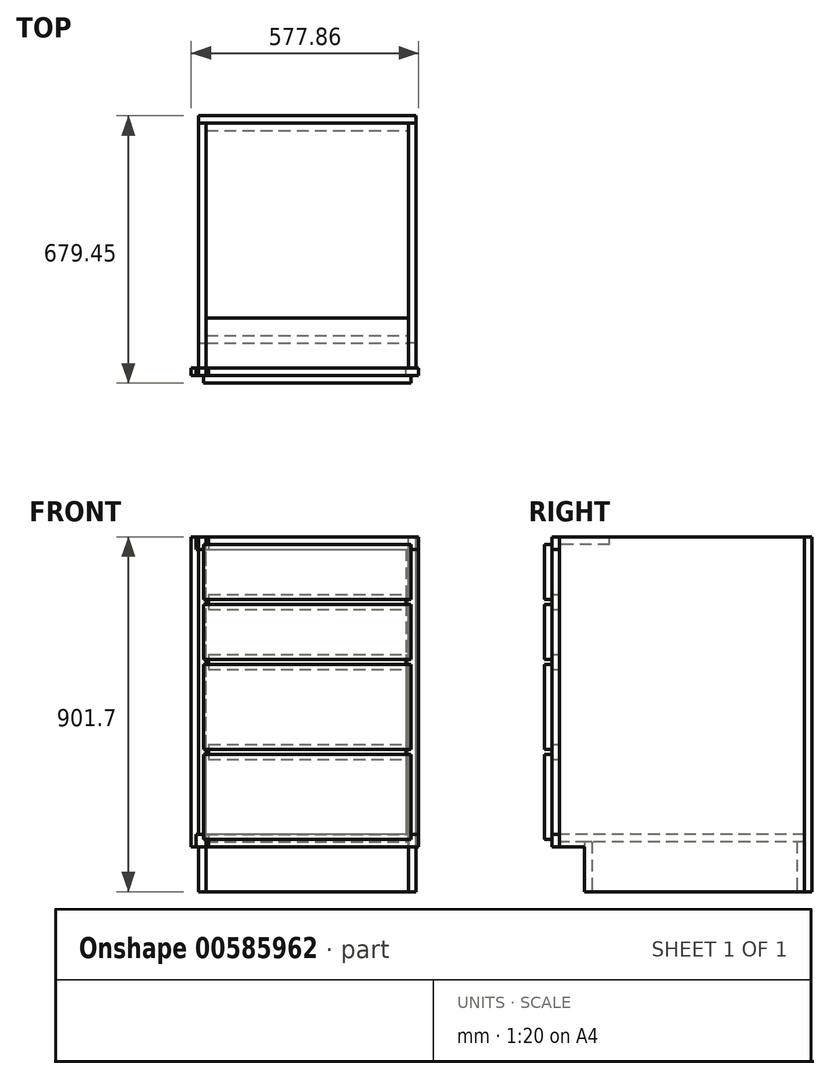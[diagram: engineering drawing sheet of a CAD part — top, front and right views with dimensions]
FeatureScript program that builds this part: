
annotation { "Feature Type Name" : "Feature", "Feature Type Description" : "" }
export const myFeature = defineFeature(function(context is Context, id is Id, definition is map)
    precondition{}
    {
        {
            var Q0;
            Q0=qCreatedBy(makeId("Top.planeOp"),FACE);
            var sketch = newSketch(context, id + "F0", { "sketchPlane" : qUnion([Q0])});
            skLineSegment(sketch, "E0.bottom", {"start": v(-257.18, 279.4) * mm, "end": v(257.18, 279.4) * mm});
            skLineSegment(sketch, "E0.top", {"start": v(-257.18, 260.35) * mm, "end": v(257.18, 260.35) * mm});
            skLineSegment(sketch, "E0.left", {"start": v(-257.18, 279.4) * mm, "end": v(-257.18, 260.35) * mm});
            skLineSegment(sketch, "E0.right", {"start": v(257.18, 279.4) * mm, "end": v(257.18, 260.35) * mm});
            skLineSegment(sketch, "E1.bottom", {"start": v(-257.18, -260.35) * mm, "end": v(257.18, -260.35) * mm});
            skLineSegment(sketch, "E1.top", {"start": v(-257.18, -279.4) * mm, "end": v(257.18, -279.4) * mm});
            skLineSegment(sketch, "E1.left", {"start": v(-257.18, -260.35) * mm, "end": v(-257.18, -279.4) * mm});
            skLineSegment(sketch, "E1.right", {"start": v(257.18, -260.35) * mm, "end": v(257.18, -279.4) * mm});
            skPoint(sketch, "E2", {"position": v(0, -260.35) * mm});
            skPoint(sketch, "E3", {"position": v(0, 260.35) * mm});
            skLineSegment(sketch, "E4", {"start": v(6.15, 279.4) * mm, "end": v(6.15, -279.4) * mm, "construction": true});
            skPoint(sketch, "E5", {"position": v(6.15, 0) * mm});
            skSolve(sketch);
        }
        {
            var Q0;
            Q0=makeQuery(id+"F0.imprint","IMPRINT",FACE,{"disambiguationData":[TD([[makeQuery(id+"F0.imprint","IMPRINT",EDGE,{"derivedFrom":sQuery(id+"F0.wireOp",EDGE,"E0.bottom")}),-1.0]])]});
            var Q1;
            Q1=makeQuery(id+"F0.imprint","IMPRINT",FACE,{"disambiguationData":[TD([[makeQuery(id+"F0.imprint","IMPRINT",EDGE,{"derivedFrom":sQuery(id+"F0.wireOp",EDGE,"E1.bottom")}),-1.0]])]});
            extrude(context, id + "F1", {"entities" : qUnion([Q0, Q1]), "depth" : 127 * mm, "offsetDistance" : 25.4 * mm});
        }
        {
            var Q0;
            Q0=makeQuery(id+"F1.opExtrude","SWEPT_FACE",FACE,{"disambiguationData":[OSD([sQuery(id+"F0.wireOp",EDGE,"E0.left")])]});
            var sketch = newSketch(context, id + "F2", { "sketchPlane" : qUnion([Q0])});
            skLineSegment(sketch, "E6.bottom", {"start": v(-279.4, 0) * mm, "end": v(342.9, 0) * mm});
            skLineSegment(sketch, "E6.top", {"start": v(-279.4, 901.7) * mm, "end": v(342.9, 901.7) * mm});
            skLineSegment(sketch, "E6.left", {"start": v(-279.4, 0) * mm, "end": v(-279.4, 901.7) * mm});
            skLineSegment(sketch, "E6.right", {"start": v(342.9, 0) * mm, "end": v(342.9, 901.7) * mm});
            skLineSegment(sketch, "E7.bottom", {"start": v(342.9, 0) * mm, "end": v(279.4, 0) * mm});
            skLineSegment(sketch, "E7.top", {"start": v(342.9, 114.3) * mm, "end": v(279.4, 114.3) * mm});
            skLineSegment(sketch, "E7.left", {"start": v(342.9, 0) * mm, "end": v(342.9, 114.3) * mm});
            skLineSegment(sketch, "E7.right", {"start": v(279.4, 0) * mm, "end": v(279.4, 114.3) * mm});
            skSolve(sketch);
        }
        {
            var Q0;
            {var subQ3=sQuery(id+"F2.wireOp",EDGE,"E6.top");Q0=makeQuery(id+"F2.imprint","IMPRINT",FACE,{"disambiguationData":[TD([[makeQuery(id+"F2.imprint","IMPRINT",EDGE,{"derivedFrom":subQ3}),-1.0]])]});}
            var Q1;
            {var subQ3=sQuery(id+"F0.wireOp",EDGE,"E0.left");var subQ5=makeQuery(id+"F1.opExtrude","CAP_EDGE",EDGE,{"disambiguationData":[OSD([subQ3])],"isStart":false});Q1=makeQuery(id+"F2.imprint","IMPRINT",FACE,{"disambiguationData":[TD([[makeQuery(id+"F2.imprint","IMPRINT",EDGE,{"derivedFrom":subQ5}),-1.0]])]});}
            extrude(context, id + "F3", {"entities" : qUnion([Q0, Q1]), "depth" : 19.05 * mm, "offsetDistance" : 25.4 * mm});
        }
        {
            var Q0;
            Q0=makeQuery(id+"F3.opExtrude","SWEPT_BODY",BODY,{"disambiguationData":[OSD([sQuery(id+"F2.wireOp",EDGE,"E6.bottom"),sQuery(id+"F2.wireOp",EDGE,"E6.top"),sQuery(id+"F2.wireOp",EDGE,"E6.left"),sQuery(id+"F2.wireOp",EDGE,"E6.right"),sQuery(id+"F2.wireOp",EDGE,"E7.top"),sQuery(id+"F2.wireOp",EDGE,"E7.right")])]});
            var Q1;
            Q1=qCreatedBy(makeId("Right.planeOp"),FACE);
            mirror(context, id + "F4", {"entities" : qUnion([Q0]), "mirrorPlane" : qUnion([Q1])});
        }
        {
            var Q0;
            Q0=makeQuery(id+"F1.opExtrude","CAP_FACE",FACE,{"disambiguationData":[OSD([sQuery(id+"F0.wireOp",EDGE,"E0.bottom"),sQuery(id+"F0.wireOp",EDGE,"E0.top"),sQuery(id+"F0.wireOp",EDGE,"E0.left"),sQuery(id+"F0.wireOp",EDGE,"E0.right")])],"isStart":false});
            var sketch = newSketch(context, id + "F5", { "sketchPlane" : qUnion([Q0])});
            skLineSegment(sketch, "E8.bottom", {"start": v(-257.18, 279.4) * mm, "end": v(257.18, 279.4) * mm});
            skLineSegment(sketch, "E8.top", {"start": v(-257.18, -342.9) * mm, "end": v(257.18, -342.9) * mm});
            skLineSegment(sketch, "E8.left", {"start": v(-257.18, 279.4) * mm, "end": v(-257.18, -342.9) * mm});
            skLineSegment(sketch, "E8.right", {"start": v(257.18, 279.4) * mm, "end": v(257.18, -342.9) * mm});
            skSolve(sketch);
        }
        {
            var Q0;
            {var subQ0=sQuery(id+"F5.wireOp",EDGE,"E8.top");Q0=makeQuery(id+"F5.imprint","IMPRINT",FACE,{"disambiguationData":[TD([[makeQuery(id+"F5.imprint","IMPRINT",EDGE,{"derivedFrom":subQ0}),1.0]])]});}
            var Q1;
            {var subQ0=sQuery(id+"F5.wireOp",EDGE,"E8.bottom");Q1=makeQuery(id+"F5.imprint","IMPRINT",FACE,{"disambiguationData":[TD([[makeQuery(id+"F5.imprint","IMPRINT",EDGE,{"derivedFrom":subQ0}),-1.0]])]});}
            extrude(context, id + "F6", {"entities" : qUnion([Q0, Q1]), "depth" : 19.05 * mm, "offsetDistance" : 25.4 * mm});
        }
        {
            var Q0;
            Q0=makeQuery(id+"F3.opExtrude","SWEPT_FACE",FACE,{"disambiguationData":[OSD([sQuery(id+"F2.wireOp",EDGE,"E6.top")])]});
            var sketch = newSketch(context, id + "F7", { "sketchPlane" : qUnion([Q0])});
            skLineSegment(sketch, "E9.bottom", {"start": v(-257.18, -342.9) * mm, "end": v(257.18, -342.9) * mm});
            skLineSegment(sketch, "E9.top", {"start": v(-257.18, -215.9) * mm, "end": v(257.18, -215.9) * mm});
            skLineSegment(sketch, "E9.left", {"start": v(-257.18, -342.9) * mm, "end": v(-257.18, -215.9) * mm});
            skLineSegment(sketch, "E9.right", {"start": v(257.18, -342.9) * mm, "end": v(257.18, -215.9) * mm});
            skLineSegment(sketch, "E10.bottom", {"start": v(-257.18, 279.4) * mm, "end": v(257.18, 279.4) * mm});
            skLineSegment(sketch, "E10.top", {"start": v(-257.18, 260.35) * mm, "end": v(257.18, 260.35) * mm});
            skLineSegment(sketch, "E10.left", {"start": v(-257.18, 279.4) * mm, "end": v(-257.18, 260.35) * mm});
            skLineSegment(sketch, "E10.right", {"start": v(257.18, 279.4) * mm, "end": v(257.18, 260.35) * mm});
            skSolve(sketch);
        }
        {
            var Q0;
            Q0=makeQuery(id+"F7.imprint","IMPRINT",FACE,{"disambiguationData":[TD([[makeQuery(id+"F7.imprint","IMPRINT",EDGE,{"derivedFrom":sQuery(id+"F7.wireOp",EDGE,"E9.bottom")}),1.0]])]});
            extrude(context, id + "F8", {"entities" : qUnion([Q0]), "oppositeDirection" : true, "depth" : 19.05 * mm, "offsetDistance" : 25.4 * mm});
        }
        {
            var Q0;
            Q0=makeQuery(id+"F3.opExtrude","SWEPT_FACE",FACE,{"disambiguationData":[OSD([sQuery(id+"F2.wireOp",EDGE,"E6.right")])]});
            var sketch = newSketch(context, id + "F9", { "sketchPlane" : qUnion([Q0])});
            skLineSegment(sketch, "E11.bottom", {"start": v(-282.58, 901.7) * mm, "end": v(282.58, 901.7) * mm});
            skLineSegment(sketch, "E11.top", {"start": v(-282.58, 869.95) * mm, "end": v(282.58, 869.95) * mm});
            skLineSegment(sketch, "E11.left", {"start": v(-282.58, 901.7) * mm, "end": v(-282.58, 869.95) * mm});
            skLineSegment(sketch, "E11.right", {"start": v(282.58, 901.7) * mm, "end": v(282.58, 869.95) * mm});
            skLineSegment(sketch, "E12.bottom", {"start": v(282.58, 114.3) * mm, "end": v(-282.58, 114.3) * mm});
            skLineSegment(sketch, "E12.top", {"start": v(282.58, 146.05) * mm, "end": v(-282.58, 146.05) * mm});
            skLineSegment(sketch, "E12.left", {"start": v(282.58, 114.3) * mm, "end": v(282.58, 146.05) * mm});
            skLineSegment(sketch, "E12.right", {"start": v(-282.58, 114.3) * mm, "end": v(-282.58, 146.05) * mm});
            skLineSegment(sketch, "E13.bottom", {"start": v(-282.58, 869.95) * mm, "end": v(-250.82, 869.95) * mm});
            skLineSegment(sketch, "E13.top", {"start": v(-282.58, 146.05) * mm, "end": v(-250.82, 146.05) * mm});
            skLineSegment(sketch, "E13.left", {"start": v(-282.58, 869.95) * mm, "end": v(-282.58, 146.05) * mm});
            skLineSegment(sketch, "E13.right", {"start": v(-250.82, 869.95) * mm, "end": v(-250.82, 146.05) * mm});
            skLineSegment(sketch, "E14.bottom", {"start": v(282.58, 869.95) * mm, "end": v(250.83, 869.95) * mm});
            skLineSegment(sketch, "E14.top", {"start": v(282.58, 146.05) * mm, "end": v(250.83, 146.05) * mm});
            skLineSegment(sketch, "E14.left", {"start": v(282.58, 869.95) * mm, "end": v(282.58, 146.05) * mm});
            skLineSegment(sketch, "E14.right", {"start": v(250.83, 869.95) * mm, "end": v(250.83, 146.05) * mm});
            skLineSegment(sketch, "E15.bottom", {"start": v(-250.82, 755.65) * mm, "end": v(250.83, 755.65) * mm});
            skLineSegment(sketch, "E15.top", {"start": v(-250.82, 717.55) * mm, "end": v(250.83, 717.55) * mm});
            skLineSegment(sketch, "E15.left", {"start": v(-250.82, 755.65) * mm, "end": v(-250.82, 717.55) * mm});
            skLineSegment(sketch, "E15.right", {"start": v(250.83, 755.65) * mm, "end": v(250.83, 717.55) * mm});
            skLineSegment(sketch, "E16.bottom", {"start": v(-250.83, 374.65) * mm, "end": v(250.83, 374.65) * mm});
            skLineSegment(sketch, "E16.top", {"start": v(-250.83, 336.55) * mm, "end": v(250.83, 336.55) * mm});
            skLineSegment(sketch, "E16.left", {"start": v(-250.82, 374.65) * mm, "end": v(-250.82, 336.55) * mm});
            skLineSegment(sketch, "E16.right", {"start": v(250.83, 374.65) * mm, "end": v(250.83, 336.55) * mm});
            skPoint(sketch, "E17", {"position": v(-250.83, 355.6) * mm});
            skLineSegment(sketch, "E18.bottom", {"start": v(-282.58, 901.7) * mm, "end": v(-250.82, 901.7) * mm});
            skLineSegment(sketch, "E18.right", {"start": v(-250.82, 901.7) * mm, "end": v(-250.82, 869.95) * mm});
            skLineSegment(sketch, "E19.top", {"start": v(282.58, 901.7) * mm, "end": v(250.83, 901.7) * mm});
            skLineSegment(sketch, "E19.left", {"start": v(282.58, 869.95) * mm, "end": v(282.58, 901.7) * mm});
            skLineSegment(sketch, "E19.right", {"start": v(250.83, 869.95) * mm, "end": v(250.83, 901.7) * mm});
            skLineSegment(sketch, "E20.bottom", {"start": v(-250.82, 146.05) * mm, "end": v(-282.58, 146.05) * mm});
            skLineSegment(sketch, "E20.top", {"start": v(-250.82, 114.3) * mm, "end": v(-282.58, 114.3) * mm});
            skLineSegment(sketch, "E20.left", {"start": v(-250.82, 146.05) * mm, "end": v(-250.82, 114.3) * mm});
            skLineSegment(sketch, "E20.right", {"start": v(-282.58, 146.05) * mm, "end": v(-282.58, 114.3) * mm});
            skLineSegment(sketch, "E21.bottom", {"start": v(250.83, 146.05) * mm, "end": v(282.58, 146.05) * mm});
            skLineSegment(sketch, "E21.top", {"start": v(250.83, 114.3) * mm, "end": v(282.58, 114.3) * mm});
            skLineSegment(sketch, "E21.left", {"start": v(250.83, 146.05) * mm, "end": v(250.83, 114.3) * mm});
            skLineSegment(sketch, "E21.right", {"start": v(282.58, 146.05) * mm, "end": v(282.58, 114.3) * mm});
            skLineSegment(sketch, "E22.bottom", {"start": v(-282.58, 901.7) * mm, "end": v(-295.28, 901.7) * mm});
            skLineSegment(sketch, "E22.top", {"start": v(-282.58, 114.3) * mm, "end": v(-295.28, 114.3) * mm});
            skLineSegment(sketch, "E22.left", {"start": v(-282.58, 901.7) * mm, "end": v(-282.58, 114.3) * mm});
            skLineSegment(sketch, "E22.right", {"start": v(-295.28, 901.7) * mm, "end": v(-295.28, 114.3) * mm});
            skLineSegment(sketch, "E23.bottom", {"start": v(-250.82, 603.25) * mm, "end": v(250.83, 603.25) * mm});
            skLineSegment(sketch, "E23.top", {"start": v(-250.82, 565.15) * mm, "end": v(250.83, 565.15) * mm});
            skLineSegment(sketch, "E23.left", {"start": v(-250.82, 603.25) * mm, "end": v(-250.82, 565.15) * mm});
            skLineSegment(sketch, "E23.right", {"start": v(250.83, 603.25) * mm, "end": v(250.83, 565.15) * mm});
            skLineSegment(sketch, "E24", {"start": v(0, 565.15) * mm, "end": v(0, 146.05) * mm, "construction": true});
            skPoint(sketch, "E25", {"position": v(0, 355.6) * mm});
            skSolve(sketch);
        }
        {
            var Q0;
            Q0=makeQuery(id+"F9.imprint","IMPRINT",FACE,{"disambiguationData":[TD([[makeQuery(id+"F9.imprint","IMPRINT",EDGE,{"derivedFrom":sQuery(id+"F9.wireOp",EDGE,"E11.bottom")}),-1.0]])]});
            extrude(context, id + "F10", {"entities" : qUnion([Q0]), "depth" : 19.05 * mm, "offsetDistance" : 25.4 * mm});
        }
        {
            var Q0;
            {var subQ1=sQuery(id+"F9.wireOp",EDGE,"E12.top");Q0=makeQuery(id+"F9.imprint","IMPRINT",FACE,{"disambiguationData":[TD([[makeQuery(id+"F9.imprint","IMPRINT",EDGE,{"derivedFrom":subQ1}),1.0]])]});}
            var Q1;
            {var subQ0=sQuery(id+"F9.wireOp",EDGE,"E12.bottom");var subQ1=sQuery(id+"F2.wireOp",EDGE,"E6.right");var subQ2=makeQuery(id+"F3.opExtrude","CAP_EDGE",EDGE,{"disambiguationData":[OSD([subQ1])],"isStart":true});var subQ3=makeQuery(id+"F9.imprint","INTERSECT",VERTEX,{"derivedFrom":[subQ2,subQ0]});var subQ4=makeQuery(id+"F3.opExtrude","CAP_EDGE",EDGE,{"disambiguationData":[OSD([subQ1])],"isStart":false});var subQ5=makeQuery(id+"F9.imprint","INTERSECT",VERTEX,{"derivedFrom":[subQ4,subQ0]});Q1=makeQuery(id+"F9.imprint","IMPRINT",FACE,{"disambiguationData":[TD([[makeQuery(id+"F9.imprint","IMPRINT",EDGE,{"disambiguationData":[TD([[subQ3,1.0],[subQ5,-1.0]])],"derivedFrom":subQ0}),1.0]])]});}
            var Q2;
            {var subQ3=sQuery(id+"F9.wireOp",EDGE,"E12.right");Q2=makeQuery(id+"F9.imprint","IMPRINT",FACE,{"disambiguationData":[TD([[makeQuery(id+"F9.imprint","IMPRINT",EDGE,{"derivedFrom":subQ3}),-1.0]])]});}
            extrude(context, id + "F11", {"entities" : qUnion([Q0, Q1, Q2]), "depth" : 19.05 * mm, "offsetDistance" : 25.4 * mm});
        }
        {
            var Q0;
            {var subQ0=sQuery(id+"F9.wireOp",EDGE,"E15.left");Q0=makeQuery(id+"F9.imprint","IMPRINT",FACE,{"disambiguationData":[TD([[makeQuery(id+"F9.imprint","IMPRINT",EDGE,{"derivedFrom":subQ0}),-1.0]])]});}
            var Q1;
            {var subQ0=sQuery(id+"F9.wireOp",EDGE,"E13.bottom");var subQ1=sQuery(id+"F2.wireOp",EDGE,"E6.right");var subQ2=makeQuery(id+"F3.opExtrude","CAP_EDGE",EDGE,{"disambiguationData":[OSD([subQ1])],"isStart":false});var subQ3=makeQuery(id+"F9.imprint","INTERSECT",VERTEX,{"derivedFrom":[subQ2,subQ0]});Q1=makeQuery(id+"F9.imprint","IMPRINT",FACE,{"disambiguationData":[TD([[makeQuery(id+"F9.imprint","IMPRINT",EDGE,{"disambiguationData":[TD([[subQ3,-1.0]])],"derivedFrom":subQ0}),-1.0]])]});}
            var Q2;
            {var subQ0=sQuery(id+"F9.wireOp",EDGE,"E13.left");Q2=makeQuery(id+"F9.imprint","IMPRINT",FACE,{"disambiguationData":[TD([[makeQuery(id+"F9.imprint","IMPRINT",EDGE,{"derivedFrom":subQ0}),1.0]])]});}
            var Q3;
            {var subQ0=sQuery(id+"F9.wireOp",EDGE,"E18.bottom");var subQ1=sQuery(id+"F2.wireOp",EDGE,"E6.right");var subQ2=makeQuery(id+"F3.opExtrude","CAP_EDGE",EDGE,{"disambiguationData":[OSD([subQ1])],"isStart":true});var subQ3=makeQuery(id+"F9.imprint","INTERSECT",VERTEX,{"derivedFrom":[subQ2,subQ0]});Q3=makeQuery(id+"F9.imprint","IMPRINT",FACE,{"disambiguationData":[TD([[makeQuery(id+"F9.imprint","IMPRINT",EDGE,{"disambiguationData":[TD([[subQ3,1.0]])],"derivedFrom":subQ0}),-1.0]])]});}
            var Q4;
            {var subQ3=sQuery(id+"F9.wireOp",EDGE,"E18.right");Q4=makeQuery(id+"F9.imprint","IMPRINT",FACE,{"disambiguationData":[TD([[makeQuery(id+"F9.imprint","IMPRINT",EDGE,{"derivedFrom":subQ3}),-1.0]])]});}
            var Q5;
            {var subQ3=sQuery(id+"F9.wireOp",EDGE,"E11.left");Q5=makeQuery(id+"F9.imprint","IMPRINT",FACE,{"disambiguationData":[TD([[makeQuery(id+"F9.imprint","IMPRINT",EDGE,{"derivedFrom":subQ3}),1.0]])]});}
            var Q6;
            {var subQ0=sQuery(id+"F9.wireOp",EDGE,"E20.left");Q6=makeQuery(id+"F9.imprint","IMPRINT",FACE,{"disambiguationData":[TD([[makeQuery(id+"F9.imprint","IMPRINT",EDGE,{"derivedFrom":subQ0}),-1.0]])]});}
            var Q7;
            {var subQ0=sQuery(id+"F9.wireOp",EDGE,"E20.bottom");var subQ1=sQuery(id+"F2.wireOp",EDGE,"E6.right");var subQ2=makeQuery(id+"F3.opExtrude","CAP_EDGE",EDGE,{"disambiguationData":[OSD([subQ1])],"isStart":true});var subQ3=makeQuery(id+"F9.imprint","INTERSECT",VERTEX,{"derivedFrom":[subQ2,subQ0]});Q7=makeQuery(id+"F9.imprint","IMPRINT",FACE,{"disambiguationData":[TD([[makeQuery(id+"F9.imprint","IMPRINT",EDGE,{"disambiguationData":[TD([[subQ3,-1.0]])],"derivedFrom":subQ0}),1.0]])]});}
            var Q8;
            {var subQ0=sQuery(id+"F9.wireOp",EDGE,"E20.right");Q8=makeQuery(id+"F9.imprint","IMPRINT",FACE,{"disambiguationData":[TD([[makeQuery(id+"F9.imprint","IMPRINT",EDGE,{"derivedFrom":subQ0}),1.0]])]});}
            var Q9;
            {var subQ0=sQuery(id+"F9.wireOp",EDGE,"E13.bottom");var subQ1=sQuery(id+"F2.wireOp",EDGE,"E6.right");var subQ2=makeQuery(id+"F3.opExtrude","CAP_EDGE",EDGE,{"disambiguationData":[OSD([subQ1])],"isStart":false});var subQ3=makeQuery(id+"F9.imprint","INTERSECT",VERTEX,{"derivedFrom":[subQ2,subQ0]});Q9=makeQuery(id+"F9.imprint","IMPRINT",FACE,{"disambiguationData":[TD([[makeQuery(id+"F9.imprint","IMPRINT",EDGE,{"disambiguationData":[TD([[subQ3,-1.0]])],"derivedFrom":subQ0}),-1.0]])]});}
            var Q10;
            {var subQ3=sQuery(id+"F9.wireOp",EDGE,"E22.bottom");Q10=makeQuery(id+"F9.imprint","IMPRINT",FACE,{"disambiguationData":[TD([[makeQuery(id+"F9.imprint","IMPRINT",EDGE,{"derivedFrom":subQ3}),1.0]])]});}
            var Q11;
            {var subQ0=sQuery(id+"F9.wireOp",EDGE,"E22.left");var subQ1=sQuery(id+"F9.wireOp",EDGE,"E13.bottom");var subQ2=makeQuery(id+"F9.imprint","INTERSECT",VERTEX,{"derivedFrom":[subQ1,subQ0]});Q11=makeQuery(id+"F9.imprint","IMPRINT",FACE,{"disambiguationData":[TD([[makeQuery(id+"F9.imprint","IMPRINT",EDGE,{"disambiguationData":[TD([[subQ2,-1.0]])],"derivedFrom":subQ1}),-1.0]])]});}
            var Q12;
            {var subQ3=sQuery(id+"F9.wireOp",EDGE,"E22.left");var subQ5=sQuery(id+"F9.wireOp",EDGE,"E13.bottom");var subQ6=makeQuery(id+"F9.imprint","INTERSECT",VERTEX,{"derivedFrom":[subQ5,subQ3]});Q12=makeQuery(id+"F9.imprint","IMPRINT",FACE,{"disambiguationData":[TD([[makeQuery(id+"F9.imprint","IMPRINT",EDGE,{"disambiguationData":[TD([[subQ6,-1.0]])],"derivedFrom":subQ5}),1.0]])]});}
            var Q13;
            {var subQ0=sQuery(id+"F9.wireOp",EDGE,"E22.left");var subQ1=sQuery(id+"F9.wireOp",EDGE,"E20.bottom");var subQ2=makeQuery(id+"F9.imprint","INTERSECT",VERTEX,{"derivedFrom":[subQ1,subQ0]});Q13=makeQuery(id+"F9.imprint","IMPRINT",FACE,{"disambiguationData":[TD([[makeQuery(id+"F9.imprint","IMPRINT",EDGE,{"disambiguationData":[TD([[subQ2,1.0]])],"derivedFrom":subQ1}),1.0]])]});}
            extrude(context, id + "F12", {"entities" : qUnion([Q0, Q1, Q2, Q3, Q4, Q5, Q6, Q7, Q8, Q9, Q10, Q11, Q12, Q13]), "depth" : 19.05 * mm, "offsetDistance" : 25.4 * mm});
        }
        {
            var Q0;
            Q0=makeQuery(id+"F9.imprint","IMPRINT",FACE,{"disambiguationData":[TD([[makeQuery(id+"F9.imprint","IMPRINT",EDGE,{"derivedFrom":sQuery(id+"F9.wireOp",EDGE,"E14.left")}),-1.0]])]});
            var Q1;
            Q1=makeQuery(id+"F9.imprint","IMPRINT",FACE,{"disambiguationData":[TD([[makeQuery(id+"F9.imprint","IMPRINT",EDGE,{"derivedFrom":sQuery(id+"F9.wireOp",EDGE,"E21.bottom")}),-1.0]])]});
            var Q2;
            Q2=makeQuery(id+"F9.imprint","IMPRINT",FACE,{"disambiguationData":[TD([[makeQuery(id+"F9.imprint","IMPRINT",EDGE,{"derivedFrom":sQuery(id+"F9.wireOp",EDGE,"E14.bottom")}),-1.0]])]});
            extrude(context, id + "F13", {"entities" : qUnion([Q0, Q1, Q2]), "depth" : 19.05 * mm, "offsetDistance" : 25.4 * mm});
        }
        {
            var Q0;
            Q0=makeQuery(id+"F9.imprint","IMPRINT",FACE,{"disambiguationData":[TD([[makeQuery(id+"F9.imprint","IMPRINT",EDGE,{"derivedFrom":sQuery(id+"F9.wireOp",EDGE,"E15.bottom")}),-1.0]])]});
            var Q1;
            Q1=makeQuery(id+"F9.imprint","IMPRINT",FACE,{"disambiguationData":[TD([[makeQuery(id+"F9.imprint","IMPRINT",EDGE,{"derivedFrom":sQuery(id+"F9.wireOp",EDGE,"E16.bottom")}),-1.0]])]});
            var Q2;
            Q2=makeQuery(id+"F9.imprint","IMPRINT",FACE,{"disambiguationData":[TD([[makeQuery(id+"F9.imprint","IMPRINT",EDGE,{"derivedFrom":sQuery(id+"F9.wireOp",EDGE,"E23.bottom")}),-1.0]])]});
            extrude(context, id + "F14", {"entities" : qUnion([Q0, Q1, Q2]), "depth" : 19.05 * mm, "offsetDistance" : 25.4 * mm});
        }
        {
            var Q0;
            Q0=makeQuery(id+"F4.opPattern","COPY",FACE,{"derivedFrom":makeQuery(id+"F3.opExtrude","SWEPT_FACE",FACE,{"disambiguationData":[OSD([sQuery(id+"F2.wireOp",EDGE,"E6.left")])]}),"instanceName":"1"});
            var sketch = newSketch(context, id + "F15", { "sketchPlane" : qUnion([Q0])});
            skLineSegment(sketch, "E26.bottom", {"start": v(-276.23, 901.7) * mm, "end": v(276.23, 901.7) * mm});
            skLineSegment(sketch, "E26.top", {"start": v(-276.23, 0) * mm, "end": v(276.23, 0) * mm});
            skLineSegment(sketch, "E26.left", {"start": v(-276.23, 901.7) * mm, "end": v(-276.23, 0) * mm});
            skLineSegment(sketch, "E26.right", {"start": v(276.23, 901.7) * mm, "end": v(276.23, 0) * mm});
            skSolve(sketch);
        }
        {
            var Q0;
            {var subQ3=sQuery(id+"F15.wireOp",EDGE,"E26.right");Q0=makeQuery(id+"F15.imprint","IMPRINT",FACE,{"disambiguationData":[TD([[makeQuery(id+"F15.imprint","IMPRINT",EDGE,{"derivedFrom":subQ3}),-1.0]])]});}
            var Q1;
            {var subQ4=sQuery(id+"F15.wireOp",EDGE,"E26.left");Q1=makeQuery(id+"F15.imprint","IMPRINT",FACE,{"disambiguationData":[TD([[makeQuery(id+"F15.imprint","IMPRINT",EDGE,{"derivedFrom":subQ4}),-1.0]])]});}
            extrude(context, id + "F16", {"entities" : qUnion([Q0, Q1]), "depth" : 19.05 * mm, "offsetDistance" : 25.4 * mm});
        }
        {
            var Q0;
            Q0=makeQuery(id+"F12.opExtrude","CAP_FACE",FACE,{"disambiguationData":[OSD([sQuery(id+"F9.wireOp",EDGE,"E13.right"),sQuery(id+"F9.wireOp",EDGE,"E15.left"),sQuery(id+"F9.wireOp",EDGE,"E16.left"),sQuery(id+"F9.wireOp",EDGE,"E18.bottom"),sQuery(id+"F9.wireOp",EDGE,"E18.right"),sQuery(id+"F9.wireOp",EDGE,"E20.top"),sQuery(id+"F9.wireOp",EDGE,"E20.left"),sQuery(id+"F9.wireOp",EDGE,"E22.bottom"),sQuery(id+"F9.wireOp",EDGE,"E22.top"),sQuery(id+"F9.wireOp",EDGE,"E22.right"),sQuery(id+"F9.wireOp",EDGE,"E23.left")])],"isStart":false});
            var sketch = newSketch(context, id + "F17", { "sketchPlane" : qUnion([Q0])});
            skLineSegment(sketch, "E27.bottom", {"start": v(-263.52, 882.65) * mm, "end": v(263.53, 882.65) * mm});
            skLineSegment(sketch, "E27.top", {"start": v(-263.52, 742.95) * mm, "end": v(263.53, 742.95) * mm});
            skLineSegment(sketch, "E27.left", {"start": v(-263.52, 882.65) * mm, "end": v(-263.52, 742.95) * mm});
            skLineSegment(sketch, "E27.right", {"start": v(263.53, 882.65) * mm, "end": v(263.53, 742.95) * mm});
            skLineSegment(sketch, "E28.bottom", {"start": v(-263.52, 730.25) * mm, "end": v(263.53, 730.25) * mm});
            skLineSegment(sketch, "E28.top", {"start": v(-263.52, 590.55) * mm, "end": v(263.53, 590.55) * mm});
            skLineSegment(sketch, "E28.left", {"start": v(-263.52, 730.25) * mm, "end": v(-263.52, 590.55) * mm});
            skLineSegment(sketch, "E28.right", {"start": v(263.53, 730.25) * mm, "end": v(263.53, 590.55) * mm});
            skLineSegment(sketch, "E29.bottom", {"start": v(263.53, 577.85) * mm, "end": v(-263.52, 577.85) * mm});
            skLineSegment(sketch, "E29.top", {"start": v(263.53, 361.95) * mm, "end": v(-263.52, 361.95) * mm});
            skLineSegment(sketch, "E29.left", {"start": v(263.53, 577.85) * mm, "end": v(263.53, 361.95) * mm});
            skLineSegment(sketch, "E29.right", {"start": v(-263.52, 577.85) * mm, "end": v(-263.52, 361.95) * mm});
            skLineSegment(sketch, "E30.bottom", {"start": v(-263.52, 349.25) * mm, "end": v(263.53, 349.25) * mm});
            skLineSegment(sketch, "E30.top", {"start": v(-263.52, 133.35) * mm, "end": v(263.53, 133.35) * mm});
            skLineSegment(sketch, "E30.left", {"start": v(-263.52, 349.25) * mm, "end": v(-263.52, 133.35) * mm});
            skLineSegment(sketch, "E30.right", {"start": v(263.53, 349.25) * mm, "end": v(263.53, 133.35) * mm});
            skSolve(sketch);
        }
        {
            var Q0;
            Q0 = qSketchRegion(id + "F17", true);
            extrude(context, id + "F18", {"entities" : qUnion([Q0]), "depth" : 19.05 * mm, "offsetDistance" : 25.4 * mm});
        }
    });
